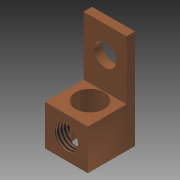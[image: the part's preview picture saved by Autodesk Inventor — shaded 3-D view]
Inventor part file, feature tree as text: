
AUTODESK INVENTOR PART (.ipt)
format: ipt  version: 2013 (Build 170138000, 138)  size: 133,120 bytes
history: native  units: mm (DEFAULTED — no unit token found)
features: sketch x4, extrude x2, hole x2
ambient origin geometry x8: Origin, YZ Plane, XZ Plane, XY Plane, X Axis, Y Axis, Z Axis, Center Point
bodies: Solid1 (feature_tree)
feature tree (8):
  extrude  "Extrusion1"  Depth=14.0mm
  extrude  "Extrusion2"  Depth=7.0mm
  hole  "Hole1"  [1 undecoded]
  hole  "Hole2"  [1 undecoded]
  sketch  "Sketch1"  dims[d0=12.75mm d1=14.0mm]
  sketch  "Sketch2"  dims[d2=6.375mm d3=7.0mm]
  sketch  "Sketch3"  dims[d4=12.0mm d5=0.0mm d7=2.5mm]
  sketch  "Sketch4"  dims[d8=17.5mm d9=0.0mm d10=8.0mm d11=6.375mm d12=6.5mm d13=6.0mm d14=4.0mm d15=2.0mm d16=14.3117mm d17=8.0mm d18=20.594885mm d19=6.375mm d20=6.0mm d21=6.917mm d22=6.0mm d23=4.0mm d24=2.0mm d25=14.3117mm d26=7.0mm d27=20.594885mm]
note: 2 required parameter values undecoded (feature->parameter linkage not recoverable at this tier; creation-order binding heuristic only, values carry confidence <= 0.55)
